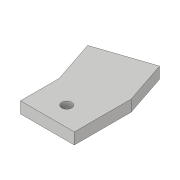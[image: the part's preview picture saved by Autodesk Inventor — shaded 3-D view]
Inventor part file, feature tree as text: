
AUTODESK INVENTOR PART (.ipt)
format: ipt  version: 2018.3 (Build 223284000, 284)  size: 114,176 bytes
history: native  units: in
note: dims shown in document units (in); Inventor stores cm internally (conversion verified against a paired STEP export)
features: extrude x2, fillet x1, sketch x1
ambient origin geometry x8: Origin, YZ Plane, XZ Plane, XY Plane, X Axis, Y Axis, Z Axis, Center Point
bodies: Solid1 (feature_tree)
feature tree (4):
  extrude  "Extrusion1"  Depth=0.875in
  extrude  "Extrusion2"  Depth=1.1003in
  fillet  "Fillet1"  Radius=1.0432in
  sketch  "Sketch1"  dims[d0=0.75in d1=0.875in d2=1.1003in d3=1.0432in d4=0.1925in d5=0.22in d6=0.0in d7=0.0625in d8=0.0in d15=0.126in d16=0.125in d17=0.126in d18=0.5216in d19=0.375in d20=1.1095in d21=0.0625in]
